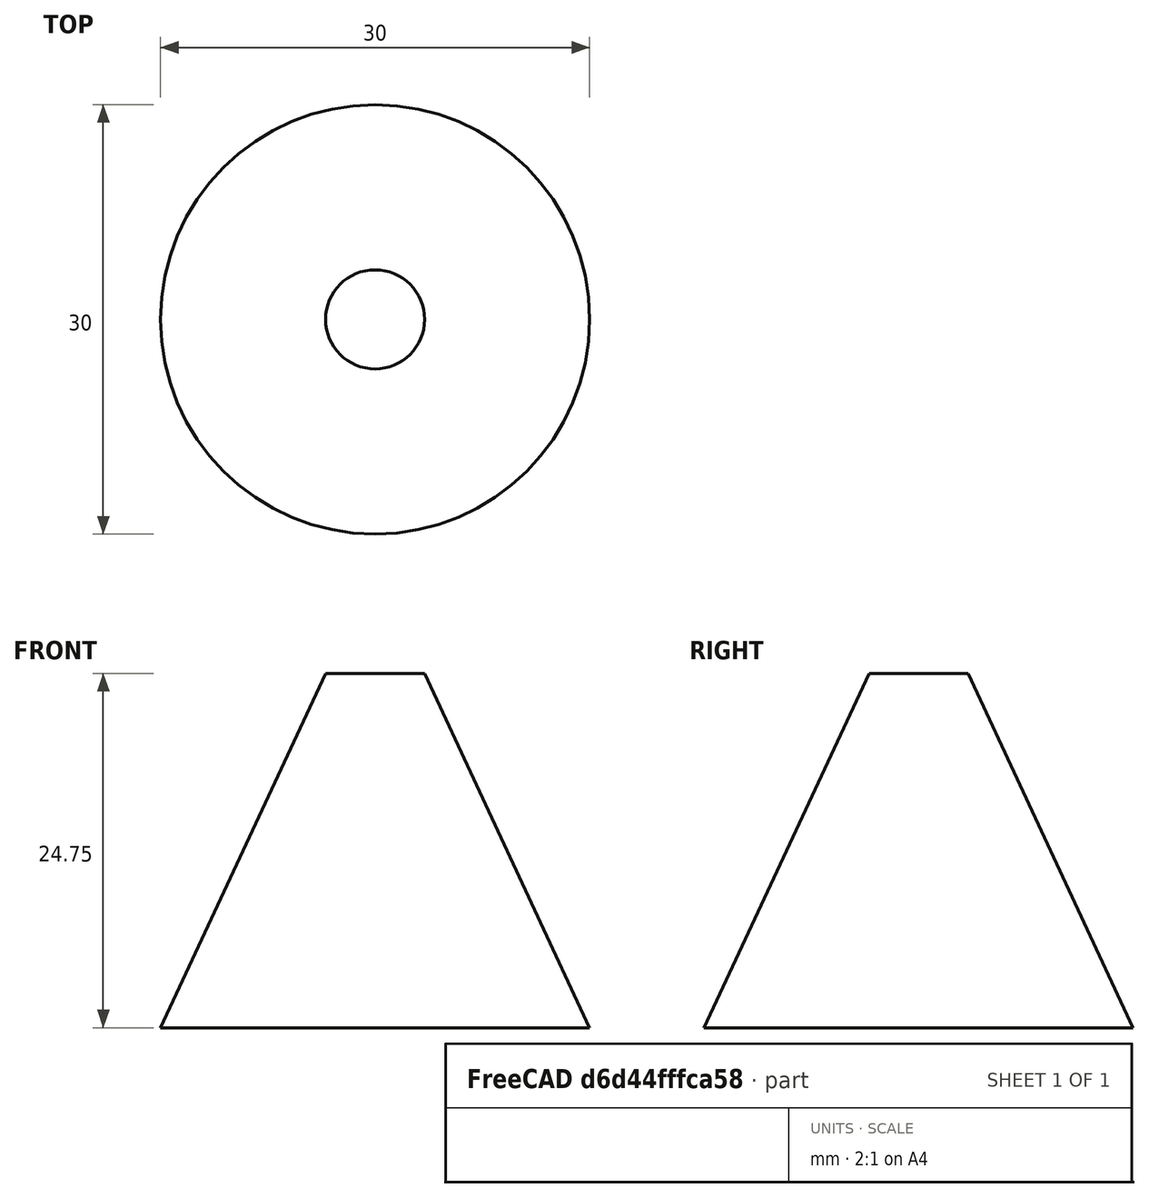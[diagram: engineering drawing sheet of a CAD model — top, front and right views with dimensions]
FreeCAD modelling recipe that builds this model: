
FCSTD DOCUMENT  (FreeCAD 0.20R29177 +233 (Git))
Label: ficha_juego_mesa
License: All rights reserved
LicenseURL: http://en.wikipedia.org/wiki/All_rights_reserved
objects: Sketcher::SketchObject×4, PartDesign::Body×2, Part::Revolution×1
note: 7 computed .brp shape members not serialized (recipe doc carries the construction recipe); baked Part::Feature solids carry a one-line shape summary decoded from their .brp

FEATURE [Sketcher::SketchObject] Sketch
  FullyConstrained = false
  Placement = pos=(0,0,0) rot=(1,0,0;1.5708rad)
  sketch-geometry (4):
    g0: LineSegment StartX=0 StartY=0 StartZ=0 EndX=2.4e-15 EndY=40 EndZ=0
    g1: LineSegment StartX=0 StartY=0 StartZ=0 EndX=15 EndY=0 EndZ=0
    g2: LineSegment StartX=15 StartY=0 StartZ=0 EndX=3.46082 EndY=24.7458 EndZ=0
    g3: ArcOfCircle CenterX=0.0888613 CenterY=32.0005 CenterZ=0 NormalX=0 NormalY=0 NormalZ=1 AngleXU=0 Radius=8 StartAngle=5.14748 EndAngle=7.86509
  constraints (11):
    c: Coincident(g0,g-1)
    c: PointOnObject(g0,g-2)
    c: Distance(g0) = 40
    c: Coincident(g1,g0)
    c: PointOnObject(g1,g-1)
    c: Distance(g1) = 15
    c: Coincident(g2,g1)
    c: Angle(g2,g1) = 1.13446
    c: Coincident(g3,g0)
    c: Coincident(g3,g2)
    c: Radius(g3) = 8
FEATURE [Sketcher::SketchObject] Sketch001
  FullyConstrained = true
  MapMode = 5
  Placement = pos=(0,0,0) rot=(1,0,0;1.5708rad)
  Support = -> [XZ_Plane]
FEATURE [Sketcher::SketchObject] Sketch002
  FullyConstrained = true
  MapMode = 5
  Placement = pos=(0,0,0) rot=(1,0,0;1.5708rad)
  Support = -> [XZ_Plane]
FEATURE [PartDesign::Body] Body
  Group = -> [Sketch001,Sketch002]
  Origin = -> Origin
FEATURE [Sketcher::SketchObject] Sketch003
  FullyConstrained = true
  MapMode = 5
  Support = -> [XY_Plane001]
FEATURE [PartDesign::Body] Body001
  Group = -> [Sketch003]
  Origin = -> Origin001
FEATURE [Part::Revolution] Revolve
  Angle = 360
  Axis = (0,0,1)
  Base = (0,0,0)
  FaceMakerClass = Part::FaceMakerBullseye
  Solid = true
  Source = -> Sketch
  Symmetric = false
